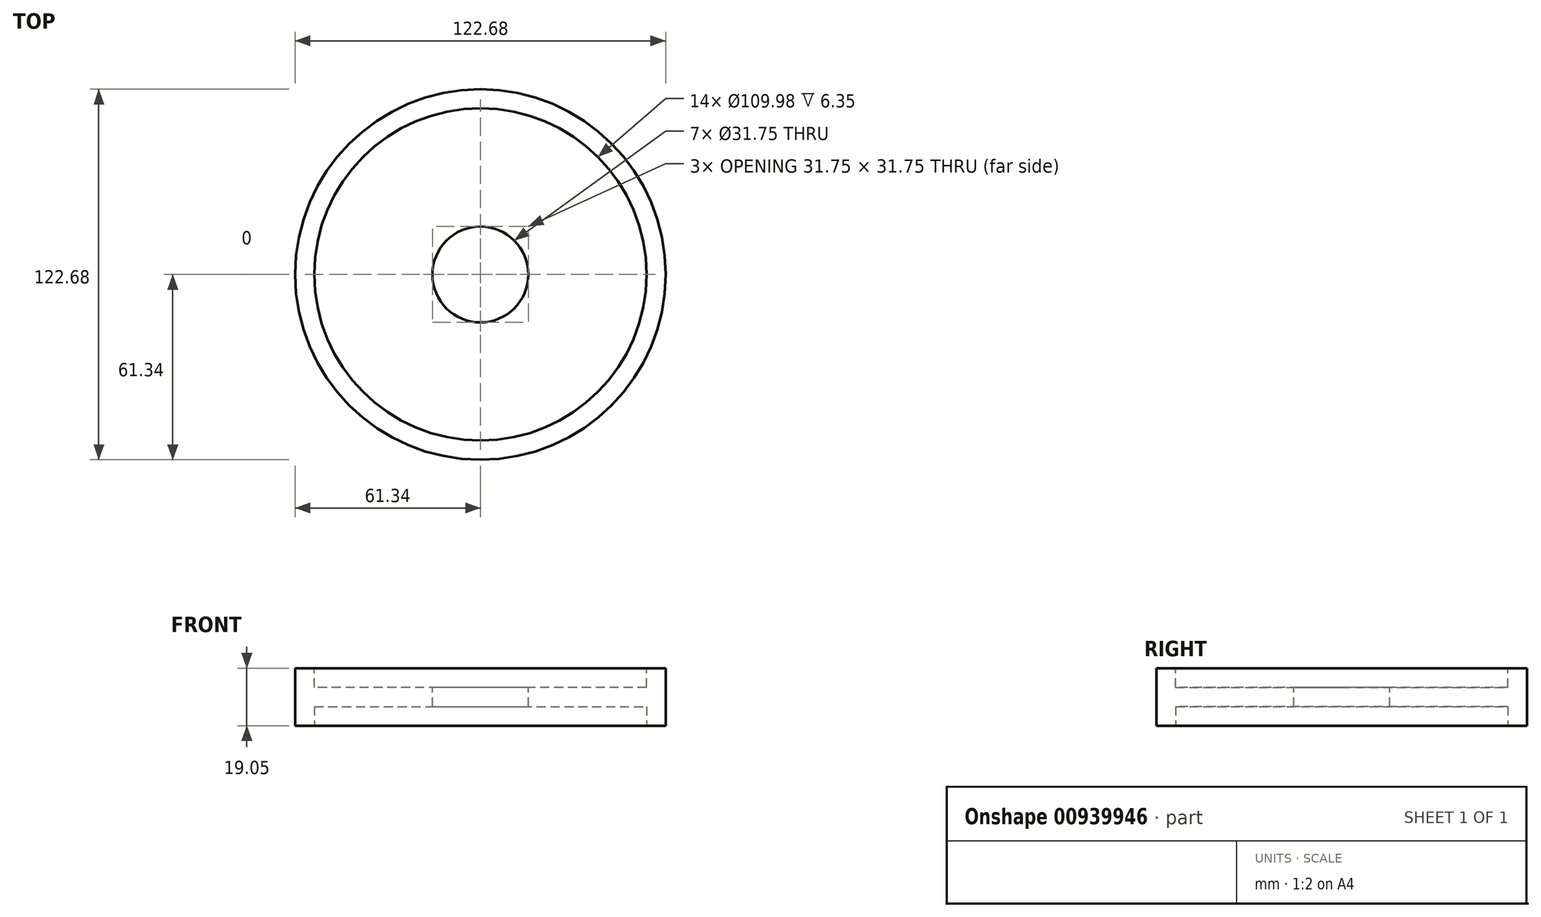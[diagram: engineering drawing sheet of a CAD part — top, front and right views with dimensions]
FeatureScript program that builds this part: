
annotation { "Feature Type Name" : "Feature", "Feature Type Description" : "" }
export const myFeature = defineFeature(function(context is Context, id is Id, definition is map)
    precondition{}
    {
        {
            var Q0;
            Q0=qCreatedBy(makeId("Top.planeOp"),FACE);
            var sketch = newSketch(context, id + "F0", { "sketchPlane" : qUnion([Q0])});
            skCircle(sketch, "E0", {"center": v(0, 0) * mm, "radius": 61.34 * mm});
            skSolve(sketch);
        }
        {
            var Q0;
            Q0=makeQuery(id+"F0.imprint","IMPRINT",FACE,{"disambiguationData":[TD([[makeQuery(id+"F0.imprint","IMPRINT",EDGE,{"derivedFrom":sQuery(id+"F0.wireOp",EDGE,"E0")}),1.0]])]});
            extrude(context, id + "F1", {"entities" : qUnion([Q0]), "depth" : 19.05 * mm, "offsetDistance" : 25.4 * mm});
        }
        {
            var Q0;
            Q0=makeQuery(id+"F1.opExtrude","CAP_FACE",FACE,{"disambiguationData":[OSD([sQuery(id+"F0.wireOp",EDGE,"E0")])],"isStart":false});
            var sketch = newSketch(context, id + "F2", { "sketchPlane" : qUnion([Q0])});
            skCircle(sketch, "E1.0", {"center": v(0, 0) * mm, "radius": 54.99 * mm});
            skSolve(sketch);
        }
        {
            var Q0;
            Q0=makeQuery(id+"F2.imprint","IMPRINT",FACE,{"disambiguationData":[TD([[makeQuery(id+"F2.imprint","IMPRINT",EDGE,{"derivedFrom":sQuery(id+"F2.wireOp",EDGE,"E1.0")}),1.0]])]});
            extrude(context, id + "F3", {"entities" : qUnion([Q0]), "operationType" : NewBodyOperationType.REMOVE, "oppositeDirection" : true, "depth" : 6.35 * mm, "offsetDistance" : 25.4 * mm});
        }
        {
            var Q0;
            Q0=makeQuery(id+"F1.opExtrude","CAP_FACE",FACE,{"disambiguationData":[OSD([sQuery(id+"F0.wireOp",EDGE,"E0")])],"isStart":true});
            var sketch = newSketch(context, id + "F4", { "sketchPlane" : qUnion([Q0])});
            skCircle(sketch, "E2.0", {"center": v(0, 0) * mm, "radius": 54.99 * mm});
            skSolve(sketch);
        }
        {
            var Q0;
            Q0=makeQuery(id+"F4.imprint","IMPRINT",FACE,{"disambiguationData":[TD([[makeQuery(id+"F4.imprint","IMPRINT",EDGE,{"derivedFrom":sQuery(id+"F4.wireOp",EDGE,"E2.0")}),1.0]])]});
            extrude(context, id + "F5", {"entities" : qUnion([Q0]), "operationType" : NewBodyOperationType.REMOVE, "oppositeDirection" : true, "depth" : 6.35 * mm, "offsetDistance" : 25.4 * mm});
        }
        {
            var Q0;
            Q0=makeQuery(id+"F3.boolean.opBoolean","COPY",FACE,{"derivedFrom":makeQuery(id+"F3.opExtrude","CAP_FACE",FACE,{"disambiguationData":[OSD([sQuery(id+"F2.wireOp",EDGE,"E1.0")])],"isStart":false})});
            var sketch = newSketch(context, id + "F6", { "sketchPlane" : qUnion([Q0])});
            skCircle(sketch, "E3", {"center": v(0, 0) * mm, "radius": 15.88 * mm});
            skSolve(sketch);
        }
        {
            var Q0;
            Q0=makeQuery(id+"F6.imprint","IMPRINT",FACE,{"disambiguationData":[TD([[makeQuery(id+"F6.imprint","IMPRINT",EDGE,{"derivedFrom":sQuery(id+"F6.wireOp",EDGE,"E3")}),1.0]])]});
            extrude(context, id + "F7", {"entities" : qUnion([Q0]), "operationType" : NewBodyOperationType.REMOVE, "endBound" : BoundingType.THROUGH_ALL, "oppositeDirection" : true, "depth" : 25.4 * mm, "offsetDistance" : 25.4 * mm});
        }
    });
